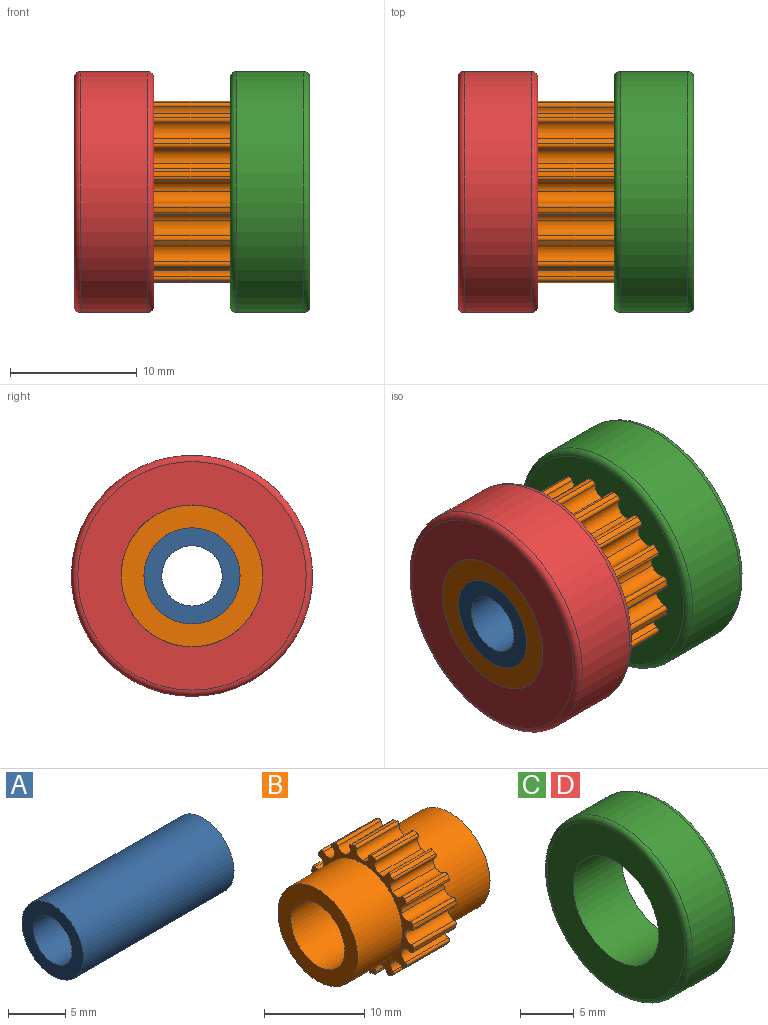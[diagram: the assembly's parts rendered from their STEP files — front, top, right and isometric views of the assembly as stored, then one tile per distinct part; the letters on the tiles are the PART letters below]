
ASSEMBLY  parts=4 mates=3
PART A: 4 faces, bbox 18.6x7.6x7.6 mm
  f0: cylinder r=2.38mm len=18.64mm, axis (-1,0,0), area 278.9mm2, adj f2,f3
  f1: cylinder r=3.8mm len=18.64mm, axis (-1,0,0), area 445.1mm2, adj f2,f3
  f2: plane 7.6x7.6mm, normal (1,0,0), area 27.6mm2, adj f0,f1
  f3: plane 7.6x7.6mm, normal (-1,0,0), area 27.6mm2, adj f0,f1
PART B: 87 faces, bbox 18.6x14.3x14.3 mm
  f0: cylinder r=0.92mm len=6.04mm, axis (-1,0,0), area 8.7mm2, adj f1,f79,f80,f81
  f1: cylinder r=0.27mm len=6.04mm, axis (-1,0,0), area 2.9mm2, adj f0,f2,f80,f81
  f2: cylinder r=7.26mm len=6.04mm, axis (-1,0,0), area 2.8mm2, adj f1,f3,f80,f81
  f3: cylinder r=0.25mm len=6.04mm, axis (-1,0,0), area 2.8mm2, adj f2,f4,f80,f81
  f4: cylinder r=0.86mm len=6.04mm, axis (-1,0,0), area 8.9mm2, adj f3,f5,f80,f81
  f5: cylinder r=0.92mm len=6.04mm, axis (-1,0,0), area 8.7mm2, adj f4,f6,f80,f81
  f6: cylinder r=0.27mm len=6.04mm, axis (-1,0,0), area 2.9mm2, adj f5,f7,f80,f81
  f7: cylinder r=7.26mm len=6.04mm, axis (-1,0,0), area 2.8mm2, adj f6,f8,f80,f81
  f8: cylinder r=0.25mm len=6.04mm, axis (-1,0,0), area 2.8mm2, adj f7,f9,f80,f81
  f9: cylinder r=0.86mm len=6.04mm, axis (-1,0,0), area 8.9mm2, adj f8,f10,f80,f81
  f10: cylinder r=0.92mm len=6.04mm, axis (-1,0,0), area 8.7mm2, adj f9,f11,f80,f81
  f11: cylinder r=0.27mm len=6.04mm, axis (-1,0,0), area 2.9mm2, adj f10,f12,f80,f81
  f12: cylinder r=7.26mm len=6.04mm, axis (-1,0,0), area 2.8mm2, adj f11,f13,f80,f81
  f13: cylinder r=0.25mm len=6.04mm, axis (-1,0,0), area 2.8mm2, adj f12,f14,f80,f81
  f14: cylinder r=0.86mm len=6.04mm, axis (-1,0,0), area 8.9mm2, adj f13,f15,f80,f81
  f15: cylinder r=0.92mm len=6.04mm, axis (-1,0,0), area 8.7mm2, adj f14,f16,f80,f81
  f16: cylinder r=0.27mm len=6.04mm, axis (-1,0,0), area 2.9mm2, adj f15,f17,f80,f81
  f17: cylinder r=7.26mm len=6.04mm, axis (-1,0,0), area 2.8mm2, adj f16,f18,f80,f81
  f18: cylinder r=0.25mm len=6.04mm, axis (-1,0,0), area 2.8mm2, adj f17,f19,f80,f81
  f19: cylinder r=0.86mm len=6.04mm, axis (-1,0,0), area 8.9mm2, adj f18,f20,f80,f81
  f20: cylinder r=0.92mm len=6.04mm, axis (-1,0,0), area 8.7mm2, adj f19,f21,f80,f81
  f21: cylinder r=0.27mm len=6.04mm, axis (-1,0,0), area 2.9mm2, adj f20,f22,f80,f81
  f22: cylinder r=7.26mm len=6.04mm, axis (-1,0,0), area 2.8mm2, adj f21,f23,f80,f81
  f23: cylinder r=0.25mm len=6.04mm, axis (-1,0,0), area 2.8mm2, adj f22,f24,f80,f81
  f24: cylinder r=0.86mm len=6.04mm, axis (-1,0,0), area 8.9mm2, adj f23,f25,f80,f81
  f25: cylinder r=0.92mm len=6.04mm, axis (-1,0,0), area 8.7mm2, adj f24,f26,f80,f81
  f26: cylinder r=0.27mm len=6.04mm, axis (-1,0,0), area 2.9mm2, adj f25,f27,f80,f81
  f27: cylinder r=7.26mm len=6.04mm, axis (-1,0,0), area 2.8mm2, adj f26,f28,f80,f81
  f28: cylinder r=0.25mm len=6.04mm, axis (-1,0,0), area 2.8mm2, adj f27,f29,f80,f81
  f29: cylinder r=0.86mm len=6.04mm, axis (-1,0,0), area 8.9mm2, adj f28,f30,f80,f81
  f30: cylinder r=0.92mm len=6.04mm, axis (-1,0,0), area 8.7mm2, adj f29,f31,f80,f81
  f31: cylinder r=0.27mm len=6.04mm, axis (-1,0,0), area 2.9mm2, adj f30,f32,f80,f81
  f32: cylinder r=7.26mm len=6.04mm, axis (-1,0,0), area 2.8mm2, adj f31,f33,f80,f81
  f33: cylinder r=0.25mm len=6.04mm, axis (-1,0,0), area 2.8mm2, adj f32,f34,f80,f81
  f34: cylinder r=0.86mm len=6.04mm, axis (-1,0,0), area 8.9mm2, adj f33,f35,f80,f81
  f35: cylinder r=0.92mm len=6.04mm, axis (-1,0,0), area 8.7mm2, adj f34,f36,f80,f81
  f36: cylinder r=0.27mm len=6.04mm, axis (-1,0,0), area 2.9mm2, adj f35,f37,f80,f81
  f37: cylinder r=7.26mm len=6.04mm, axis (-1,0,0), area 2.8mm2, adj f36,f38,f80,f81
  f38: cylinder r=0.25mm len=6.04mm, axis (-1,0,0), area 2.8mm2, adj f37,f39,f80,f81
  f39: cylinder r=0.86mm len=6.04mm, axis (-1,0,0), area 8.9mm2, adj f38,f40,f80,f81
  f40: cylinder r=0.92mm len=6.04mm, axis (-1,0,0), area 8.7mm2, adj f39,f41,f80,f81
  f41: cylinder r=0.27mm len=6.04mm, axis (-1,0,0), area 2.9mm2, adj f40,f42,f80,f81
  f42: cylinder r=7.26mm len=6.04mm, axis (-1,0,0), area 2.8mm2, adj f41,f43,f80,f81
  f43: cylinder r=0.25mm len=6.04mm, axis (-1,0,0), area 2.8mm2, adj f42,f44,f80,f81
  f44: cylinder r=0.86mm len=6.04mm, axis (-1,0,0), area 8.9mm2, adj f43,f45,f80,f81
  f45: cylinder r=0.92mm len=6.04mm, axis (-1,0,0), area 8.7mm2, adj f44,f46,f80,f81
  f46: cylinder r=0.27mm len=6.04mm, axis (-1,0,0), area 2.9mm2, adj f45,f47,f80,f81
  f47: cylinder r=7.26mm len=6.04mm, axis (-1,0,0), area 2.8mm2, adj f46,f48,f80,f81
  f48: cylinder r=0.25mm len=6.04mm, axis (-1,0,0), area 2.8mm2, adj f47,f49,f80,f81
  f49: cylinder r=0.86mm len=6.04mm, axis (-1,0,0), area 8.9mm2, adj f48,f50,f80,f81
  f50: cylinder r=0.92mm len=6.04mm, axis (-1,0,0), area 8.7mm2, adj f49,f51,f80,f81
  f51: cylinder r=0.27mm len=6.04mm, axis (-1,0,0), area 2.9mm2, adj f50,f52,f80,f81
  f52: cylinder r=7.26mm len=6.04mm, axis (-1,0,0), area 2.8mm2, adj f51,f53,f80,f81
  f53: cylinder r=0.25mm len=6.04mm, axis (-1,0,0), area 2.8mm2, adj f52,f54,f80,f81
  f54: cylinder r=0.86mm len=6.04mm, axis (-1,0,0), area 8.9mm2, adj f53,f55,f80,f81
  f55: cylinder r=0.92mm len=6.04mm, axis (-1,0,0), area 8.7mm2, adj f54,f56,f80,f81
  f56: cylinder r=0.27mm len=6.04mm, axis (-1,0,0), area 2.9mm2, adj f55,f57,f80,f81
  f57: cylinder r=7.26mm len=6.04mm, axis (-1,0,0), area 2.8mm2, adj f56,f58,f80,f81
  f58: cylinder r=0.25mm len=6.04mm, axis (-1,0,0), area 2.8mm2, adj f57,f59,f80,f81
  f59: cylinder r=0.86mm len=6.04mm, axis (-1,0,0), area 8.9mm2, adj f58,f60,f80,f81
  f60: cylinder r=0.92mm len=6.04mm, axis (-1,0,0), area 8.7mm2, adj f59,f61,f80,f81
  f61: cylinder r=0.27mm len=6.04mm, axis (-1,0,0), area 2.9mm2, adj f60,f62,f80,f81
  f62: cylinder r=7.26mm len=6.04mm, axis (-1,0,0), area 2.8mm2, adj f61,f63,f80,f81
  f63: cylinder r=0.25mm len=6.04mm, axis (-1,0,0), area 2.8mm2, adj f62,f64,f80,f81
  f64: cylinder r=0.86mm len=6.04mm, axis (-1,0,0), area 8.9mm2, adj f63,f65,f80,f81
  f65: cylinder r=0.92mm len=6.04mm, axis (-1,0,0), area 8.7mm2, adj f64,f66,f80,f81
  f66: cylinder r=0.27mm len=6.04mm, axis (-1,0,0), area 2.9mm2, adj f65,f67,f80,f81
  f67: cylinder r=7.26mm len=6.04mm, axis (-1,0,0), area 2.8mm2, adj f66,f68,f80,f81
  f68: cylinder r=0.25mm len=6.04mm, axis (-1,0,0), area 2.8mm2, adj f67,f69,f80,f81
  f69: cylinder r=0.86mm len=6.04mm, axis (-1,0,0), area 8.9mm2, adj f68,f70,f80,f81
  f70: cylinder r=0.92mm len=6.04mm, axis (-1,0,0), area 8.7mm2, adj f69,f71,f80,f81
  f71: cylinder r=0.27mm len=6.04mm, axis (-1,0,0), area 2.9mm2, adj f70,f72,f80,f81
  f72: cylinder r=7.26mm len=6.04mm, axis (-1,0,0), area 2.8mm2, adj f71,f73,f80,f81
  f73: cylinder r=0.25mm len=6.04mm, axis (-1,0,0), area 2.8mm2, adj f72,f74,f80,f81
  f74: cylinder r=0.86mm len=6.04mm, axis (-1,0,0), area 8.9mm2, adj f73,f75,f80,f81
  f75: cylinder r=0.92mm len=6.04mm, axis (-1,0,0), area 8.7mm2, adj f74,f76,f80,f81
  f76: cylinder r=0.27mm len=6.04mm, axis (-1,0,0), area 2.9mm2, adj f75,f77,f80,f81
  f77: cylinder r=7.26mm len=6.04mm, axis (-1,0,0), area 2.8mm2, adj f76,f78,f80,f81
  f78: cylinder r=0.25mm len=6.04mm, axis (-1,0,0), area 2.8mm2, adj f77,f79,f80,f81
  f79: cylinder r=0.86mm len=6.04mm, axis (-1,0,0), area 8.9mm2, adj f0,f78,f80,f81
  f80: plane 14.34x14.34mm, normal (1,0,0), area 35mm2, adj f0,f1,f2,f3,f4,f5,f6,f7
  f81: plane 14.34x14.34mm, normal (-1,0,0), area 35mm2, adj f0,f1,f2,f3,f4,f5,f6,f7
  f82: cylinder r=3.8mm len=18.64mm, axis (1,0,0), area 444.7mm2, adj f84,f86
  f83: cylinder r=5.6mm len=11.2mm, axis (1,0,0), area 221.7mm2, adj f81,f84
  f84: plane 11.2x11.2mm, normal (-1,0,0), area 53.2mm2, adj f82,f83
  f85: cylinder r=5.6mm len=11.2mm, axis (-1,0,0), area 221.7mm2, adj f80,f86
  f86: plane 11.2x11.2mm, normal (1,0,0), area 53.2mm2, adj f82,f85
PART C: 6 faces, bbox 6.3x20.6x20.6 mm
  f0: cylinder r=5.6mm len=11.2mm, axis (-1,0,0), area 221.7mm2, adj f2,f3
  f1: cylinder r=9.53mm len=19.05mm, axis (-1,0,0), area 317.2mm2, adj f4,f5
  f2: plane 18.05x18.05mm, normal (1,0,0), area 157.4mm2, adj f0,f5
  f3: plane 18.05x18.05mm, normal (-1,0,0), area 157.4mm2, adj f0,f4
  f4: torus R=9.03mm, axis (1,0,0), area 46.1mm2, adj f1,f3
  f5: torus R=9.03mm, axis (1,0,0), area 46.1mm2, adj f1,f2
PART D: same geometry as C
PLACE A t=(-4.81,2.3,-6.35)mm fixed
PLACE B t=(1.49,2.3,-6.35)mm
PLACE C t=(7.53,2.3,-6.35)mm
PLACE D t=(-4.81,2.3,-6.35)mm
MATE fastened C.f0 <-> A.f1  axis (1,0,0) through (13.83,2.3,-6.35)mm
MATE fastened D.f0 <-> A.f0  axis (-1,0,0) through (-4.81,2.3,-6.35)mm
MATE fastened B.f85 <-> A.f1  axis (1,0,0) through (13.83,2.3,-6.35)mm
